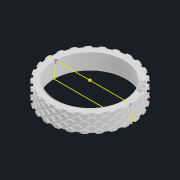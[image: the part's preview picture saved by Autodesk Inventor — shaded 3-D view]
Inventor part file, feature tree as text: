
AUTODESK INVENTOR PART (.ipt)
format: ipt  version: 2021.3 (Build 253353000, 353)  size: 1,625,600 bytes
history: native  units: mm
features: helix x6, sketch x5, extrude x2, pattern_circular x2, draft x1, projected_geometry x1
ambient origin geometry x8: Origin, YZ Plane, XZ Plane, XY Plane, X Axis, Y Axis, Z Axis, Center Point
bodies: Solid1 (feature_tree)
feature tree (17):
  extrude  "Extrusion1"  Depth=6.52mm TaperAngle=0.0deg
  draft  "FaceDraft1"
  sketch  "Sketch2"  dims[d7=4.0mm d8=9.0mm d9=10.0mm d10=1.047198mm d11=90.0deg d12=90.0deg d13=0.0mm d14=0.0mm d15=4.0mm d16=3.0mm d17=10.0mm d18=-1.047198mm d19=90.0deg d20=90.0deg d21=0.0mm d22=0.0mm d23=3.0mm]
  sketch  "Sketch4"  dims[d52=70.0mm d53=9.0mm d54=10.0mm d55=0.0mm d56=90.0deg d57=90.0deg d58=0.0mm d59=0.0mm d60=70.0mm d61=9.0mm d62=10.0mm d63=0.0mm d64=90.0deg d65=90.0deg d66=0.0mm d67=0.0mm d68=250.0mm d69=360.0deg]
  helix  "Coil1"  [1 undecoded]
  helix  "Coil2"  [1 undecoded]
  sketch  "Sketch7"  dims[d71=70.0mm d72=9.0mm d73=10.0mm d74=0.0mm d75=90.0deg d76=90.0deg d77=0.0mm d78=0.0mm d79=70.0mm d80=9.0mm d81=10.0mm d82=0.0mm d83=90.0deg d84=90.0deg d85=0.0mm d86=0.0mm d87=250.0mm d88=360.0deg d91=0.8mm d92=0.0mm]
  helix  "Coil6"  [1 undecoded]
  helix  "Coil7"  [1 undecoded]
  pattern_circular  "Circular Pattern1"  [2 undecoded]
  helix  "Coil8"  [1 undecoded]
  helix  "Coil9"  [1 undecoded]
  pattern_circular  "Circular Pattern2"  [2 undecoded]
  extrude  "Extrusion2"  [1 undecoded]
  sketch  "Sketch1"  dims[d0=26.5mm d2=6.52mm d3=0.0mm d4=1.047198mm]
  sketch  "Sketch9"
  projected_geometry  "Projected Loop1"
note: 11 required parameter values undecoded (feature->parameter linkage not recoverable at this tier; creation-order binding heuristic only, values carry confidence <= 0.55)
